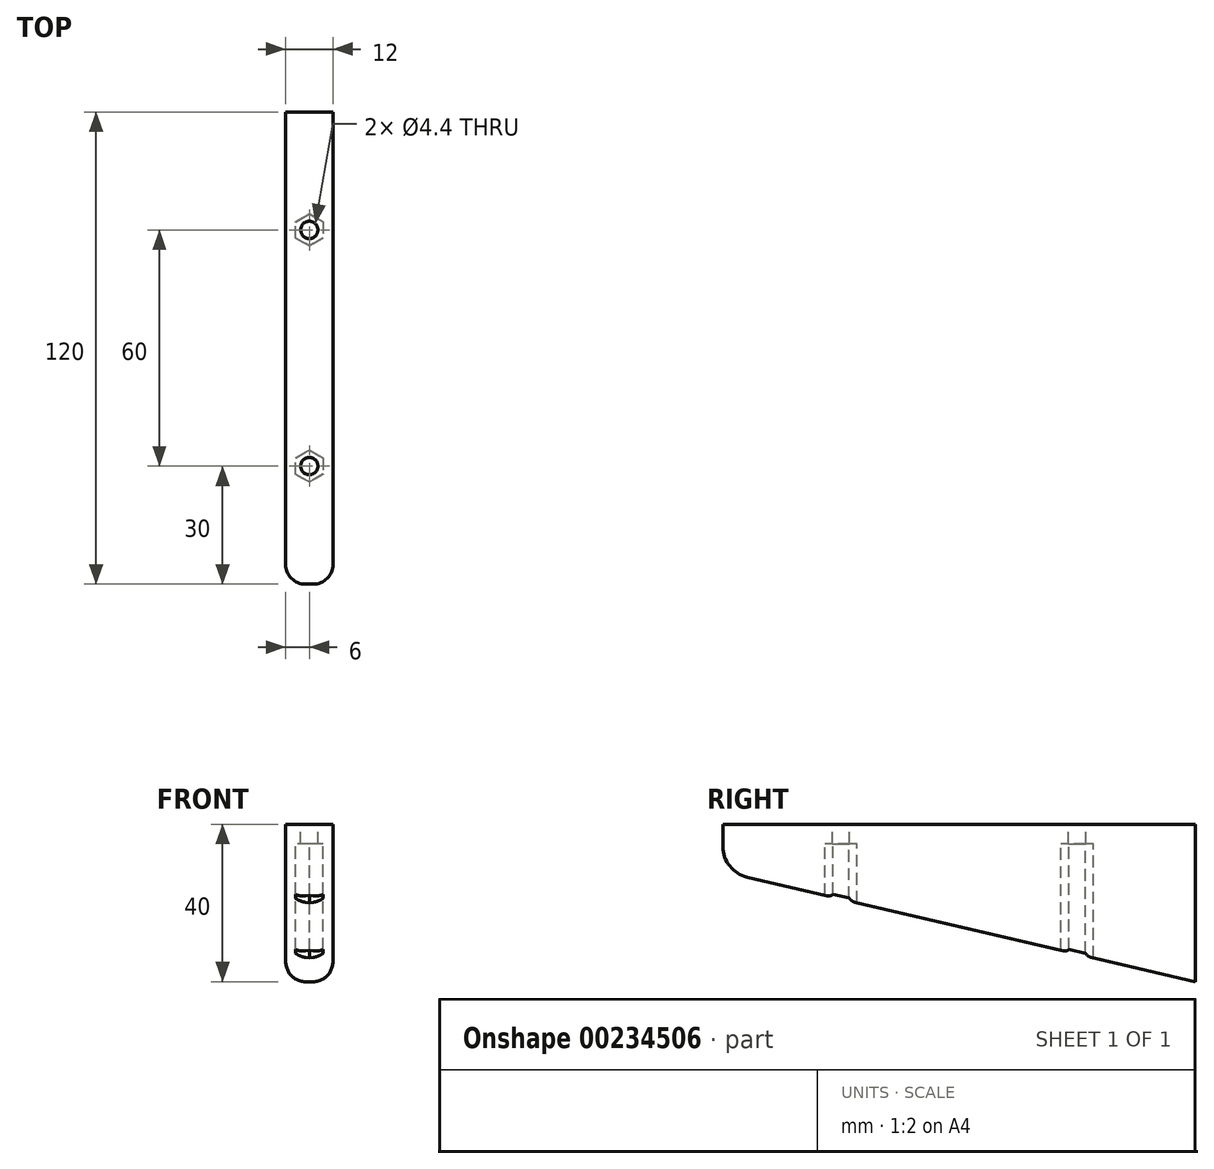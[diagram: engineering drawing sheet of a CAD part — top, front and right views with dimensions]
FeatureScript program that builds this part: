
annotation { "Feature Type Name" : "Feature", "Feature Type Description" : "" }
export const myFeature = defineFeature(function(context is Context, id is Id, definition is map)
    precondition{}
    {
        {
            var Q0;
            Q0=qCreatedBy(makeId("Right.planeOp"),FACE);
            var sketch = newSketch(context, id + "F0", { "sketchPlane" : qUnion([Q0])});
            skLineSegment(sketch, "E0", {"start": v(0, 0) * mm, "end": v(-120, 0) * mm});
            skLineSegment(sketch, "E1", {"start": v(-120, 0) * mm, "end": v(-120, -5.65) * mm});
            skLineSegment(sketch, "E2", {"start": v(-113.82, -13.44) * mm, "end": v(0, -40) * mm});
            skLineSegment(sketch, "E3", {"start": v(0, -40) * mm, "end": v(0, 0) * mm});
            skPoint(sketch, "E4.visualSharp", {"position": v(-120, -12) * mm});
            skArc(sketch, "E4.filletArc", {"start": v(-120, -5.65) * mm, "mid": v(-118.27, -10.62) * mm, "end": v(-113.82, -13.44) * mm});
            skSolve(sketch);
        }
        {
            var Q0;
            Q0 = qSketchRegion(id + "F0", true);
            extrude(context, id + "F1", {"entities" : qUnion([Q0]), "depth" : 12 * mm, "offsetDistance" : 25 * mm});
        }
        {
            var Q0;
            Q0=makeQuery(id+"F1.opExtrude","CAP_EDGE",EDGE,{"disambiguationData":[OSD([sQuery(id+"F0.wireOp",EDGE,"E2")])],"isStart":true});
            var Q1;
            Q1=makeQuery(id+"F1.opExtrude","CAP_EDGE",EDGE,{"disambiguationData":[OSD([sQuery(id+"F0.wireOp",EDGE,"E2")])],"isStart":false});
            fillet(context, id + "F2", {"entities" : qUnion([Q0, Q1]), "tangentPropagation" : true, "radius" : 5 * mm, "defaultsChanged" : false, "vertexSettings" : [], "allowEdgeOverflow" : false});
        }
        {
            var Q0;
            Q0=makeQuery(id+"F1.opExtrude","SWEPT_FACE",FACE,{"disambiguationData":[OSD([sQuery(id+"F0.wireOp",EDGE,"E0")])]});
            var sketch = newSketch(context, id + "F3", { "sketchPlane" : qUnion([Q0])});
            skCircle(sketch, "E5", {"center": v(6, -30) * mm, "radius": 2.2 * mm});
            skCircle(sketch, "E6", {"center": v(6, -90) * mm, "radius": 2.2 * mm});
            skSolve(sketch);
        }
        {
            var Q0;
            Q0 = qSketchRegion(id + "F3", true);
            extrude(context, id + "F4", {"entities" : qUnion([Q0]), "operationType" : NewBodyOperationType.REMOVE, "endBound" : BoundingType.THROUGH_ALL, "oppositeDirection" : true, "depth" : 25 * mm, "offsetDistance" : 25 * mm});
        }
        {
            var Q0;
            Q0=makeQuery(id+"F1.opExtrude","SWEPT_FACE",FACE,{"disambiguationData":[OSD([sQuery(id+"F0.wireOp",EDGE,"E0")])]});
            var sketch = newSketch(context, id + "F5", { "sketchPlane" : qUnion([Q0])});
            skCircle(sketch, "E7.cCircle", {"center": v(6, -30) * mm, "radius": 3.55 * mm, "construction": true});
            skLineSegment(sketch, "E7.0", {"start": v(6, -34.1) * mm, "end": v(2.45, -32.05) * mm});
            skLineSegment(sketch, "E7.1", {"start": v(2.45, -32.05) * mm, "end": v(2.45, -27.95) * mm});
            skLineSegment(sketch, "E7.2", {"start": v(2.45, -27.95) * mm, "end": v(6, -25.9) * mm});
            skLineSegment(sketch, "E7.3", {"start": v(6, -25.9) * mm, "end": v(9.55, -27.95) * mm});
            skLineSegment(sketch, "E7.4", {"start": v(9.55, -27.95) * mm, "end": v(9.55, -32.05) * mm});
            skLineSegment(sketch, "E7.5", {"start": v(9.55, -32.05) * mm, "end": v(6, -34.1) * mm});
            skPoint(sketch, "E7.0.midPoint", {"position": v(6, -33.55) * mm});
            skCircle(sketch, "E8.cCircle", {"center": v(6, -90) * mm, "radius": 3.55 * mm, "construction": true});
            skLineSegment(sketch, "E8.0", {"start": v(6, -94.1) * mm, "end": v(2.45, -92.05) * mm});
            skLineSegment(sketch, "E8.1", {"start": v(2.45, -92.05) * mm, "end": v(2.45, -87.95) * mm});
            skLineSegment(sketch, "E8.2", {"start": v(2.45, -87.95) * mm, "end": v(6, -85.9) * mm});
            skLineSegment(sketch, "E8.3", {"start": v(6, -85.9) * mm, "end": v(9.55, -87.95) * mm});
            skLineSegment(sketch, "E8.4", {"start": v(9.55, -87.95) * mm, "end": v(9.55, -92.05) * mm});
            skLineSegment(sketch, "E8.5", {"start": v(9.55, -92.05) * mm, "end": v(6, -94.1) * mm});
            skPoint(sketch, "E8.0.midPoint", {"position": v(6, -93.55) * mm});
            skSolve(sketch);
        }
        {
            var Q0;
            Q0 = qSketchRegion(id + "F5", true);
            extrude(context, id + "F6", {"entities" : qUnion([Q0]), "operationType" : NewBodyOperationType.REMOVE, "endBound" : BoundingType.THROUGH_ALL, "oppositeDirection" : true, "depth" : 25 * mm, "offsetDistance" : 25 * mm, "hasSecondDirection" : true, "secondDirectionOppositeDirection" : true, "secondDirectionDepth" : 5 * mm});
        }
    });
